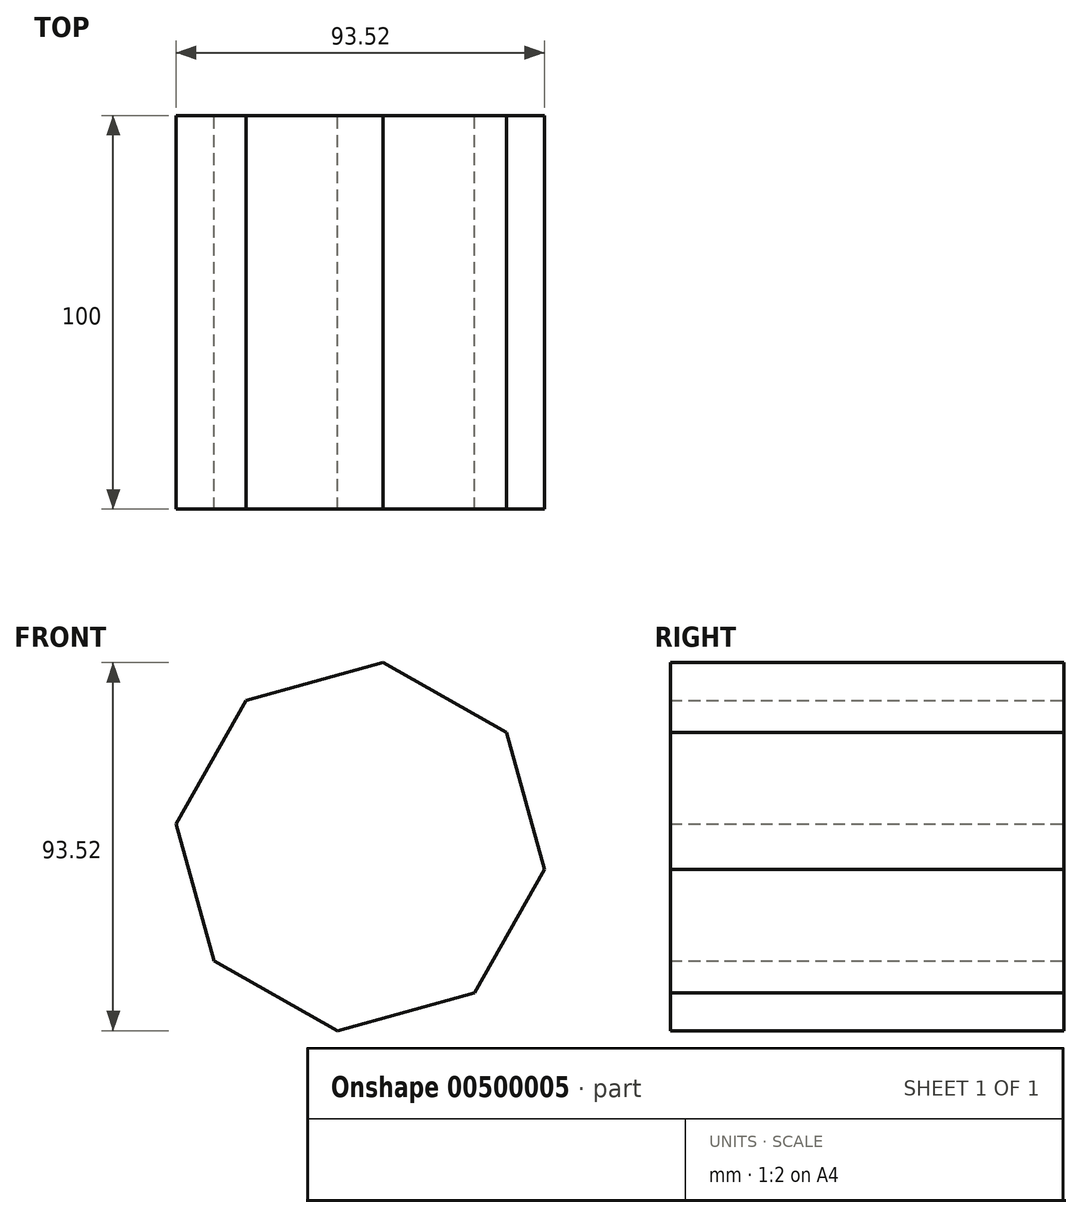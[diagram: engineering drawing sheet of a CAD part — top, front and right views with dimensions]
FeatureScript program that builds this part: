
annotation { "Feature Type Name" : "Feature", "Feature Type Description" : "" }
export const myFeature = defineFeature(function(context is Context, id is Id, definition is map)
    precondition{}
    {
        {
            var Q0;
            Q0=qCreatedBy(makeId("Front.planeOp"),FACE);
            var sketch = newSketch(context, id + "F0", { "sketchPlane" : qUnion([Q0])});
            skCircle(sketch, "E0.cCircle", {"center": v(0, 0) * mm, "radius": 47.11 * mm, "construction": true});
            skLineSegment(sketch, "E0.0", {"start": v(-28.98, 37.15) * mm, "end": v(5.78, 46.76) * mm});
            skLineSegment(sketch, "E0.1", {"start": v(5.78, 46.76) * mm, "end": v(37.15, 28.98) * mm});
            skLineSegment(sketch, "E0.2", {"start": v(37.15, 28.98) * mm, "end": v(46.76, -5.78) * mm});
            skLineSegment(sketch, "E0.3", {"start": v(46.76, -5.78) * mm, "end": v(28.98, -37.15) * mm});
            skLineSegment(sketch, "E0.4", {"start": v(28.98, -37.15) * mm, "end": v(-5.78, -46.76) * mm});
            skLineSegment(sketch, "E0.5", {"start": v(-5.78, -46.76) * mm, "end": v(-37.15, -28.98) * mm});
            skLineSegment(sketch, "E0.6", {"start": v(-37.15, -28.98) * mm, "end": v(-46.76, 5.78) * mm});
            skLineSegment(sketch, "E0.7", {"start": v(-46.76, 5.78) * mm, "end": v(-28.98, 37.15) * mm});
            skSolve(sketch);
        }
        {
            var Q0;
            Q0 = qSketchRegion(id + "F0", true);
            extrude(context, id + "F1", {"entities" : qUnion([Q0]), "endBound" : BoundingType.SYMMETRIC, "depth" : 100 * mm});
        }
    });
